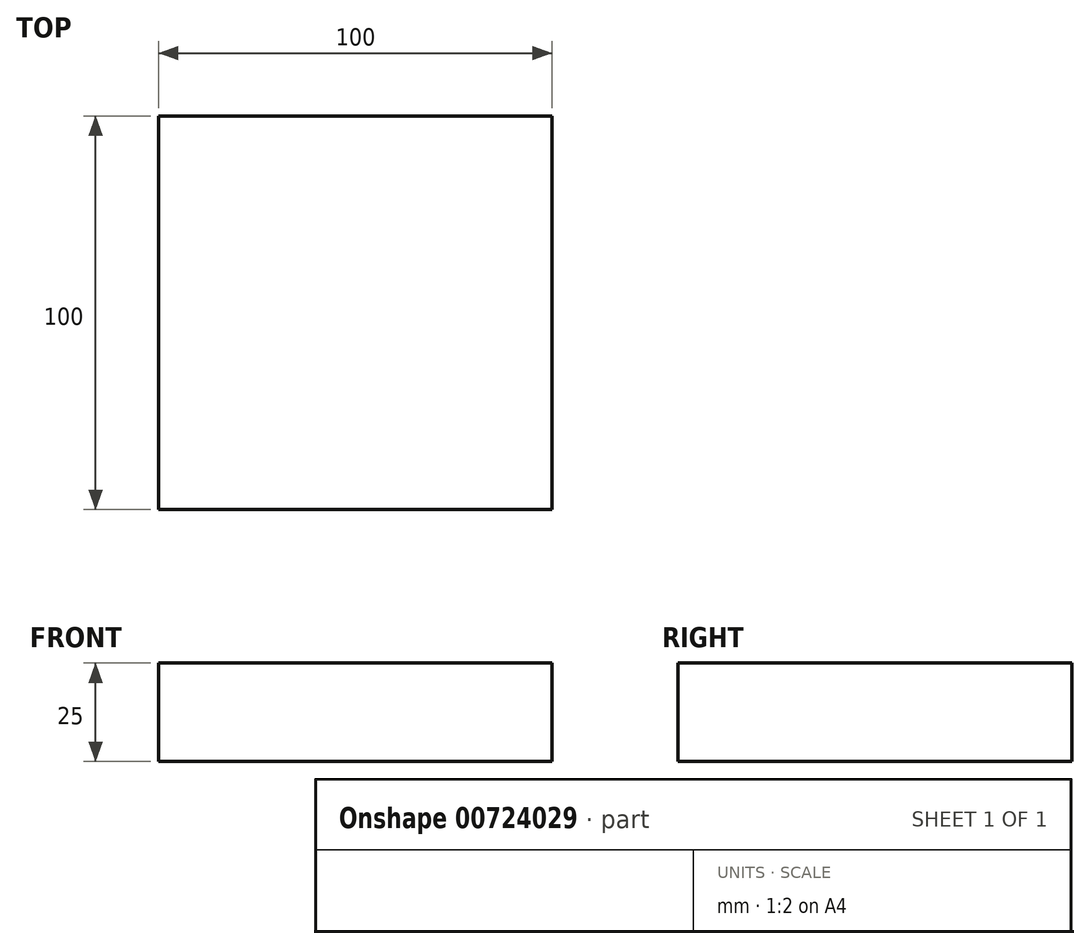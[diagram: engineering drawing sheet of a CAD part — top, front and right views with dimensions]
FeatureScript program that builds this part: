
annotation { "Feature Type Name" : "Feature", "Feature Type Description" : "" }
export const myFeature = defineFeature(function(context is Context, id is Id, definition is map)
    precondition{}
    {
        {
            var Q0;
            Q0=qCreatedBy(makeId("Top.planeOp"),FACE);
            var sketch = newSketch(context, id + "F0", { "sketchPlane" : qUnion([Q0])});
            skLineSegment(sketch, "E0.bottom", {"start": v(0, 0) * mm, "end": v(0, 0) * mm});
            skLineSegment(sketch, "E1.bottom", {"start": v(0, 0) * mm, "end": v(100, 0) * mm});
            skLineSegment(sketch, "E1.top", {"start": v(0, -100) * mm, "end": v(100, -100) * mm});
            skLineSegment(sketch, "E1.left", {"start": v(0, 0) * mm, "end": v(0, -100) * mm});
            skLineSegment(sketch, "E1.right", {"start": v(100, 0) * mm, "end": v(100, -100) * mm});
            skSolve(sketch);
        }
        {
            var Q0;
            Q0=makeQuery(id+"F0.imprint","IMPRINT",FACE,{"disambiguationData":[TD([[makeQuery(id+"F0.imprint","IMPRINT",EDGE,{"derivedFrom":sQuery(id+"F0.wireOp",EDGE,"E1.bottom")}),-1.0]])]});
            extrude(context, id + "F1", {"entities" : qUnion([Q0]), "depth" : 25 * mm, "offsetDistance" : 25 * mm});
        }
    });
